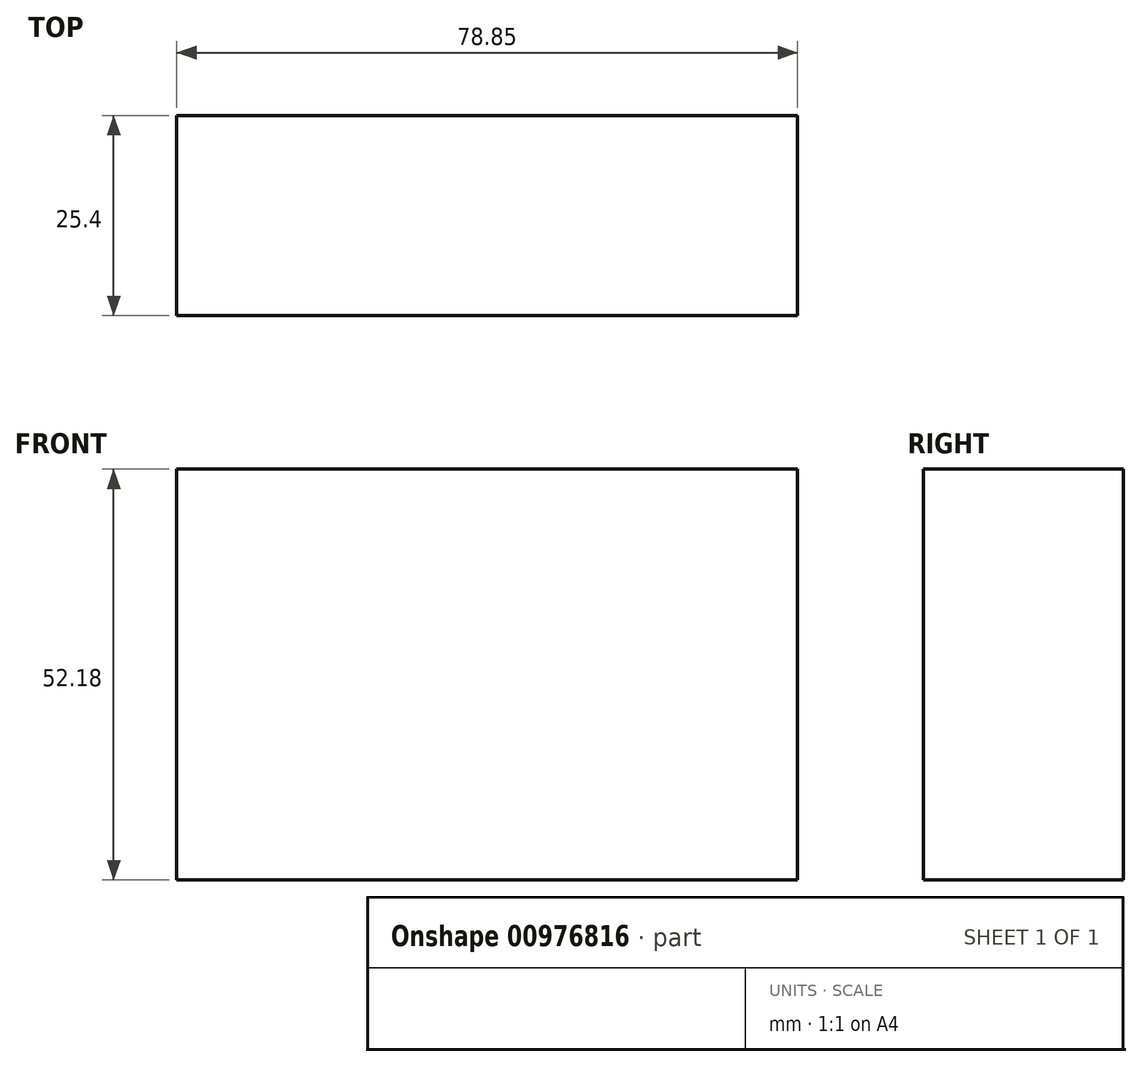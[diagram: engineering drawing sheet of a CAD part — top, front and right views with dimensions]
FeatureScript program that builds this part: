
annotation { "Feature Type Name" : "Feature", "Feature Type Description" : "" }
export const myFeature = defineFeature(function(context is Context, id is Id, definition is map)
    precondition{}
    {
        {
            var Q0;
            Q0=qCreatedBy(makeId("Front.planeOp"),FACE);
            var sketch = newSketch(context, id + "F0", { "sketchPlane" : qUnion([Q0])});
            skLineSegment(sketch, "E0", {"start": v(-51.46, 41.02) * mm, "end": v(27.4, 41.02) * mm});
            skLineSegment(sketch, "E1", {"start": v(27.4, 41.02) * mm, "end": v(27.4, -11.16) * mm});
            skLineSegment(sketch, "E2", {"start": v(27.4, -11.16) * mm, "end": v(-51.46, -11.16) * mm});
            skLineSegment(sketch, "E3", {"start": v(-51.46, 41.02) * mm, "end": v(-51.46, -11.16) * mm});
            skSolve(sketch);
        }
        {
            var Q0;
            Q0 = qSketchRegion(id + "F0", true);
            extrude(context, id + "F1", {"entities" : qUnion([Q0]), "depth" : 25.4 * mm, "offsetDistance" : 25.4 * mm});
        }
    });
